# Revit family: LOROWERK 00805-070X
name_source: partatom
category: Pipe Fittings
revit_build: Autodesk Revit 2017 (Build: 20160225_1515(x64)
units: mm (PartAtom-declared; Revit-internal decimal feet)

## family parameters
Always vertical = Yes
Cut with Voids When Loaded = No
Part Type = Breaks Into
Round Connector Dimension = Use Diameter
Shared = No
Work Plane-Based = No

## types (1)
- LOROWERK 00805-070X
    BIM = https://media.stage.bim.site
    Benennung Text = LORO-X Verschlussstopfen mit Schraubverschluss, DN70
    Brandschutzklasse Text = B1 nach DIN 4102
    CONNECTOR0_DIAMETER_dZ_0r = 70 mm
    CONNECTOR0_dZ_01 = 5 mm  [stored 0.0164042 ft]
    CONNECTOR0_ref_dZ = 5 mm  [stored 0.0164042 ft]
    DATANORM = 00805.070X
    Description = LORO-X Stahlabflussrohre
    Formstück-Gewicht [kg] Number = 0.1
    GTIN = 4038088028902
    HAN = 00805.070X
    HeinzeBIM = https://www.heinze.de
    Index Number = 2
    Manufacturer = LOROWERK K.H. Vahlbrauk GmbH & Co. KG
    Nenndruck Text = 0.5
    Nenndrucksystem Text = PN
    Nennweitensystem Text = DN
    Normen/Regeln/Zulassungen Text = DVGW für Trinkwasser
    Produktbezeichnung Text = LORO-X Stahlabflussrohre
    Produktkennung Text = Rohr
    Produktname Text = LORO-X Verschlussstopfen mit Schraubverschluss
    Produktvideo = https://media.stage.bim.site
    Querschnittsform Text = rund
    Type Name = LORO-X Verschlussstopfen mit Schraubverschluss
    VDIBSN = 020001???001001???00100100000100300700000000000140000000000000000002
    Verbindungsart I Text = Pressen
    Verbindungsart II Text = axial pressen
    Verlegeart Text = Unterputz
    max. zul. Dauer-Betriebstemperatur [°C] Number = 95

note: [stored X ft] marks values corroborated as IEEE doubles in the binary element streams (Revit-internal decimal feet)

## geometry (parser evidence)
native form markers: Blend x2
no freeform markers — native parametric forms only
